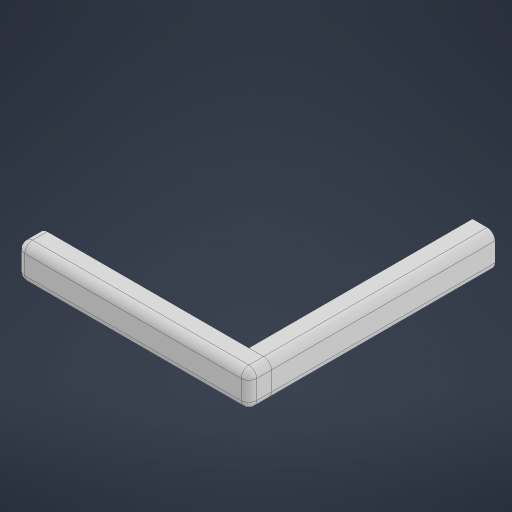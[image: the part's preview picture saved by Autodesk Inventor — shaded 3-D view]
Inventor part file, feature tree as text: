
AUTODESK INVENTOR PART (.ipt)
format: ipt  version: 2023 (Build 270158000, 158)  size: 200,704 bytes
history: native  units: in
note: dims shown in document units (in); Inventor stores cm internally (conversion verified against a paired STEP export)
features: extrude x2, sketch x2, fillet x1
ambient origin geometry x8: Origin, YZ Plane, XZ Plane, XY Plane, X Axis, Y Axis, Z Axis, Center Point
bodies: Solid1 (feature_tree), Solid2 (feature_tree)
feature tree (5):
  extrude  "Extrusion1"  Depth=3.25in
  extrude  "Extrusion2"  Depth=3.25in
  fillet  "Fillet1"  Radius=5.0in
  sketch  "Sketch1"  dims[d0=5.0in d1=3.25in]
  sketch  "Sketch2"  dims[d4=33.5in d5=0.0in d8=3.25in d9=5.0in d10=32.31in d11=0.0in d12=1.125in]
